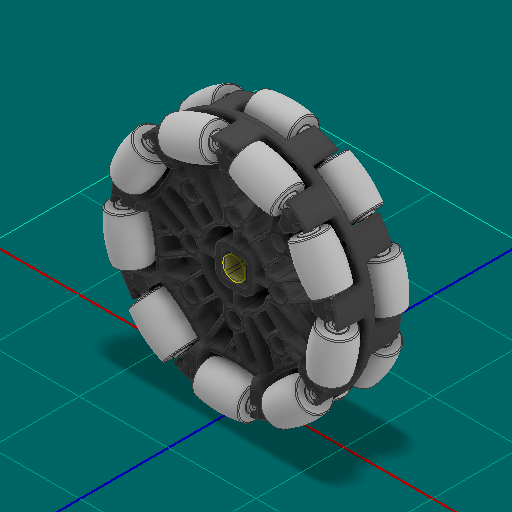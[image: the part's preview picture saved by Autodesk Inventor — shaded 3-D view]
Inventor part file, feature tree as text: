
AUTODESK INVENTOR PART (.ipt)
format: ipt  version: 2025 (Build 290162000, 162)  size: 28,622,848 bytes
history: native  units: in
note: dims shown in document units (in); Inventor stores cm internally (conversion verified against a paired STEP export)
features: other x59, sketch x1
ambient origin geometry x8: Origin, YZ Plane, XZ Plane, XY Plane, X Axis, Y Axis, Z Axis, Center Point
bodies: Solid1 (feature_tree), Solid2 (feature_tree), Solid3 (feature_tree), Solid4 (feature_tree), Solid5 (feature_tree), Solid6 (feature_tree), Solid7 (feature_tree), Solid8 (feature_tree), Solid9 (feature_tree), Solid10 (feature_tree), Solid11 (feature_tree), Solid12 (feature_tree), Solid13 (feature_tree), Solid14 (feature_tree), Solid15 (feature_tree), Solid16 (feature_tree), Solid17 (feature_tree), Solid18 (feature_tree), Solid19 (feature_tree), Solid20 (feature_tree), Solid21 (feature_tree), Solid22 (feature_tree), Solid23 (feature_tree), Solid24 (feature_tree), Solid25 (feature_tree), Solid26 (feature_tree), Solid27 (feature_tree), Solid28 (feature_tree), Solid29 (feature_tree), Solid30 (feature_tree), Solid31 (feature_tree), Solid32 (feature_tree), Solid33 (feature_tree), Solid34 (feature_tree), Solid35 (feature_tree), Solid36 (feature_tree), Solid37 (feature_tree), Solid38 (feature_tree), Solid39 (feature_tree), Solid40 (feature_tree), Solid41 (feature_tree), Solid42 (feature_tree), Solid43 (feature_tree), Solid44 (feature_tree), Solid45 (feature_tree), Solid46 (feature_tree), Solid47 (feature_tree), Solid48 (feature_tree), Solid49 (feature_tree), Solid50 (feature_tree), Solid51 (feature_tree), Solid52 (feature_tree), Solid53 (feature_tree), Solid54 (feature_tree), Solid55 (feature_tree)
feature tree (60):
  other  "2.75 Omni Antistatic.ipt"
  other  "Solid1::2.75 Omni Antistatic.ipt"
  other  "Solid2::2.75 Omni Antistatic.ipt"
  other  "Solid3::2.75 Omni Antistatic.ipt"
  other  "Solid4::2.75 Omni Antistatic.ipt"
  other  "Solid5::2.75 Omni Antistatic.ipt"
  other  "Solid6::2.75 Omni Antistatic.ipt"
  other  "Solid7::2.75 Omni Antistatic.ipt"
  other  "Solid8::2.75 Omni Antistatic.ipt"
  other  "Solid9::2.75 Omni Antistatic.ipt"
  other  "Solid10::2.75 Omni Antistatic.ipt"
  other  "Solid11::2.75 Omni Antistatic.ipt"
  other  "Solid12::2.75 Omni Antistatic.ipt"
  other  "Solid13::2.75 Omni Antistatic.ipt"
  other  "Solid14::2.75 Omni Antistatic.ipt"
  other  "Solid15::2.75 Omni Antistatic.ipt"
  other  "Solid16::2.75 Omni Antistatic.ipt"
  other  "Solid17::2.75 Omni Antistatic.ipt"
  other  "Solid18::2.75 Omni Antistatic.ipt"
  other  "Solid19::2.75 Omni Antistatic.ipt"
  other  "Solid20::2.75 Omni Antistatic.ipt"
  other  "Solid21::2.75 Omni Antistatic.ipt"
  other  "Solid22::2.75 Omni Antistatic.ipt"
  other  "Solid23::2.75 Omni Antistatic.ipt"
  other  "Solid24::2.75 Omni Antistatic.ipt"
  other  "Solid25::2.75 Omni Antistatic.ipt"
  other  "Solid26::2.75 Omni Antistatic.ipt"
  other  "Solid27::2.75 Omni Antistatic.ipt"
  other  "Solid28::2.75 Omni Antistatic.ipt"
  other  "Solid29::2.75 Omni Antistatic.ipt"
  other  "Solid30::2.75 Omni Antistatic.ipt"
  other  "Solid31::2.75 Omni Antistatic.ipt"
  other  "Solid32::2.75 Omni Antistatic.ipt"
  other  "Solid33::2.75 Omni Antistatic.ipt"
  other  "Solid34::2.75 Omni Antistatic.ipt"
  other  "Solid35::2.75 Omni Antistatic.ipt"
  other  "Solid36::2.75 Omni Antistatic.ipt"
  other  "Solid37::2.75 Omni Antistatic.ipt"
  other  "Solid38::2.75 Omni Antistatic.ipt"
  other  "Solid39::2.75 Omni Antistatic.ipt"
  other  "Solid40::2.75 Omni Antistatic.ipt"
  other  "Solid41::2.75 Omni Antistatic.ipt"
  other  "Solid42::2.75 Omni Antistatic.ipt"
  other  "Solid43::2.75 Omni Antistatic.ipt"
  other  "Solid44::2.75 Omni Antistatic.ipt"
  other  "Solid45::2.75 Omni Antistatic.ipt"
  other  "Solid46::2.75 Omni Antistatic.ipt"
  other  "Solid47::2.75 Omni Antistatic.ipt"
  other  "Solid48::2.75 Omni Antistatic.ipt"
  other  "Solid49::2.75 Omni Antistatic.ipt"
  other  "Solid50::2.75 Omni Antistatic.ipt"
  other  "Solid51::2.75 Omni Antistatic.ipt"
  other  "Solid52::2.75 Omni Antistatic.ipt"
  other  "Solid53::2.75 Omni Antistatic.ipt"
  other  "Solid54::2.75 Omni Antistatic.ipt"
  other  "Solid55::2.75 Omni Antistatic.ipt"
  other  "TaggingFeature1"
  sketch  "Sketch1"  dims[d0=0.3937in]
  other  "Srf1"
  other  "Srf1::Derived"
